# Revit family: fire_rinnai_symmetry3611_premium
name_source: partatom
category: Specialty Equipment
revit_build: Autodesk Revit 2015 (Build: 20140905_0730(x64)
units: mm (PartAtom-declared; Revit-internal decimal feet)

## types (1)
- symmetry3611_premium
    Description = Rinnai Symmetry 3611 Premium
    Manufacturer = Rinnai NZ Ltd
    Model = Symmetry 3611 Premium
    URL = www.rinnai.co.nz
    _dirpath = 04_symmetry3611
    _fire_centrewidth = 850 mm  [stored 2.78871 ft]
    _fire_clearceiling = 1000 mm  [stored 3.28084 ft]
    _fire_cleardepth = 1000 mm  [stored 3.28084 ft]
    _fire_clearheight = 400 mm  [stored 1.31234 ft]
    _fire_clearwidth = 1700 mm  [stored 5.57743 ft]
    _fire_side_clearance = 400 mm  [stored 1.31234 ft]
    _fire_top = 740 mm  [stored 2.42782 ft]
    _fire_width = 1155 mm  [stored 3.78937 ft]
    _fire_window_top = 600 mm
    _fire_window_width = 900 mm  [stored 2.95276 ft]
    _opening_depth = 540 mm  [stored 1.77165 ft]
    _opening_height = 850 mm  [stored 2.78871 ft]
    _opening_width = 1125 mm
    _rinnai_product = Fires
    clearance = 5 mm  [stored 0.0164042 ft]
    m_plinth = <By Category>
    opening floor offset = 2 mm  [stored 0.00656168 ft]
    v_fireplace = Yes

note: [stored X ft] marks values corroborated as IEEE doubles in the binary element streams (Revit-internal decimal feet)

## geometry (parser evidence)
native form markers: Sweep x13
no freeform markers — native parametric forms only
